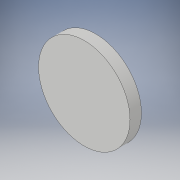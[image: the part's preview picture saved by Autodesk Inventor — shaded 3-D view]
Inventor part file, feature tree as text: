
AUTODESK INVENTOR PART (.ipt)
format: ipt  version: 2017 (Build 210142000, 142)  size: 90,112 bytes
history: native  units: in
note: dims shown in document units (in); Inventor stores cm internally (conversion verified against a paired STEP export)
features: extrude x1, sketch x1
ambient origin geometry x8: Origin, YZ Plane, XZ Plane, XY Plane, X Axis, Y Axis, Z Axis, Center Point
bodies: Solid1 (feature_tree)
feature tree (2):
  extrude  "Extrusion1"  Depth=0.5in TaperAngle=0.0deg
  sketch  "Sketch1"  dims[d0=4.0in d1=0.5in d2=0.0in]
